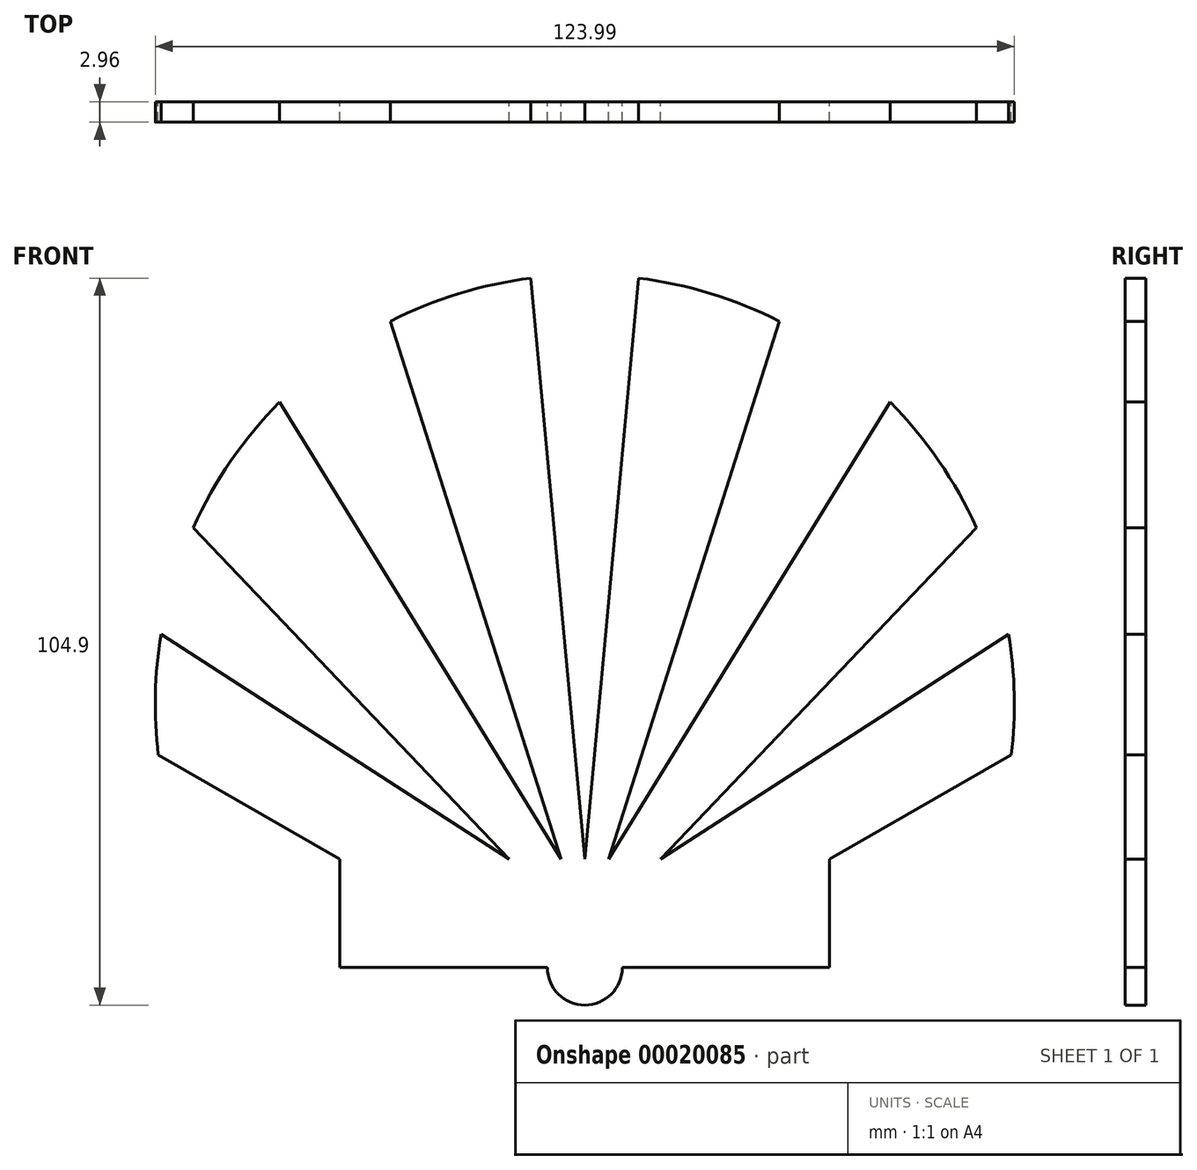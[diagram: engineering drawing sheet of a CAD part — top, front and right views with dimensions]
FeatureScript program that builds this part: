
annotation { "Feature Type Name" : "Feature", "Feature Type Description" : "" }
export const myFeature = defineFeature(function(context is Context, id is Id, definition is map)
    precondition{}
    {
        {
            var Q0;
            Q0=qCreatedBy(makeId("Front.planeOp"),FACE);
            var sketch = newSketch(context, id + "F0", { "sketchPlane" : qUnion([Q0])});
            skArc(sketch, "E0", {"start": v(-13.26, 83.85) * mm, "mid": v(-23.67, 81.61) * mm, "end": v(-33.55, 77.63) * mm});
            skLineSegment(sketch, "E1", {"start": v(-67.05, 15.05) * mm, "end": v(-40.82, 0) * mm});
            skLineSegment(sketch, "E2", {"start": v(-40.82, 0) * mm, "end": v(-40.82, -15.64) * mm});
            skLineSegment(sketch, "E3", {"start": v(-40.82, -15.64) * mm, "end": v(-10.89, -15.64) * mm});
            skPoint(sketch, "E4.orphan", {"position": v(56.07, 15.05) * mm});
            skArc(sketch, "E5", {"start": v(-10.89, -15.64) * mm, "mid": v(-9.3, -19.46) * mm, "end": v(-5.49, -21.05) * mm});
            skLineSegment(sketch, "E6", {"start": v(-66.65, 32.44) * mm, "end": v(-16.43, 0) * mm});
            skLineSegment(sketch, "E7", {"start": v(-62, 47.83) * mm, "end": v(-16.43, 0) * mm});
            skPoint(sketch, "E8.start.orphan", {"position": v(-35.12, 0) * mm});
            skLineSegment(sketch, "E9", {"start": v(-8.9, 0) * mm, "end": v(-49.54, 65.97) * mm});
            skLineSegment(sketch, "E10", {"start": v(-8.9, 0) * mm, "end": v(-33.55, 77.63) * mm});
            skLineSegment(sketch, "E11", {"start": v(-16.43, 0) * mm, "end": v(-16.43, 0) * mm});
            skLineSegment(sketch, "E12.trimOffspring", {"start": v(-8.9, 0) * mm, "end": v(0, 0) * mm});
            skArc(sketch, "E13.trimOffspring", {"start": v(-66.65, 32.44) * mm, "mid": v(-67.46, 23.76) * mm, "end": v(-67.05, 15.05) * mm});
            skArc(sketch, "E14.trimOffspring", {"start": v(-49.54, 65.97) * mm, "mid": v(-56.58, 57.46) * mm, "end": v(-62, 47.83) * mm});
            skLineSegment(sketch, "E15", {"start": v(-5.49, 0) * mm, "end": v(-13.26, 83.85) * mm});
            skLineSegment(sketch, "E16", {"start": v(-5.49, 22.35) * mm, "end": v(-5.49, -36.05) * mm});
            skArc(sketch, "E17.MirrorCS", {"start": v(-0.09, -15.64) * mm, "mid": v(-1.67, -19.46) * mm, "end": v(-5.49, -21.05) * mm});
            skLineSegment(sketch, "E18.MirrorCS", {"start": v(-2.08, 0) * mm, "end": v(38.56, 65.97) * mm});
            skLineSegment(sketch, "E19.MirrorCS", {"start": v(-2.08, 0) * mm, "end": v(22.57, 77.63) * mm});
            skLineSegment(sketch, "E20.MirrorCS", {"start": v(-5.49, 0) * mm, "end": v(2.29, 83.85) * mm});
            skLineSegment(sketch, "E21.MirrorCS", {"start": v(51.02, 47.83) * mm, "end": v(5.45, 0) * mm});
            skLineSegment(sketch, "E22.MirrorCS", {"start": v(55.68, 32.44) * mm, "end": v(5.45, 0) * mm});
            skArc(sketch, "E23.MirrorCS", {"start": v(38.56, 65.97) * mm, "mid": v(45.6, 57.46) * mm, "end": v(51.02, 47.83) * mm});
            skPoint(sketch, "E24.MirrorP", {"position": v(24.15, 0) * mm});
            skArc(sketch, "E25.MirrorCS", {"start": v(55.68, 32.44) * mm, "mid": v(56.49, 23.76) * mm, "end": v(56.07, 15.05) * mm});
            skLineSegment(sketch, "E26.MirrorCS", {"start": v(29.85, -15.64) * mm, "end": v(-0.09, -15.64) * mm});
            skArc(sketch, "E27.MirrorCS", {"start": v(2.29, 83.85) * mm, "mid": v(12.7, 81.61) * mm, "end": v(22.57, 77.63) * mm});
            skLineSegment(sketch, "E28.MirrorCS", {"start": v(56.07, 15.05) * mm, "end": v(29.85, 0) * mm});
            skLineSegment(sketch, "E29.MirrorCS", {"start": v(29.85, 0) * mm, "end": v(29.85, -15.64) * mm});
            skSolve(sketch);
        }
        {
            var Q0;
            Q0 = qSketchRegion(id + "F0", true);
            var Q1;
            Q1=makeQuery(id+"F0.imprint","IMPRINT",FACE,{"disambiguationData":[TD([[makeQuery(id+"F0.imprint","IMPRINT",EDGE,{"derivedFrom":sQuery(id+"F0.wireOp",EDGE,"E1")}),1.0]])]});
            extrude(context, id + "F1", {"entities" : qUnion([Q0, Q1]), "depth" : 2.96 * mm});
        }
    });
